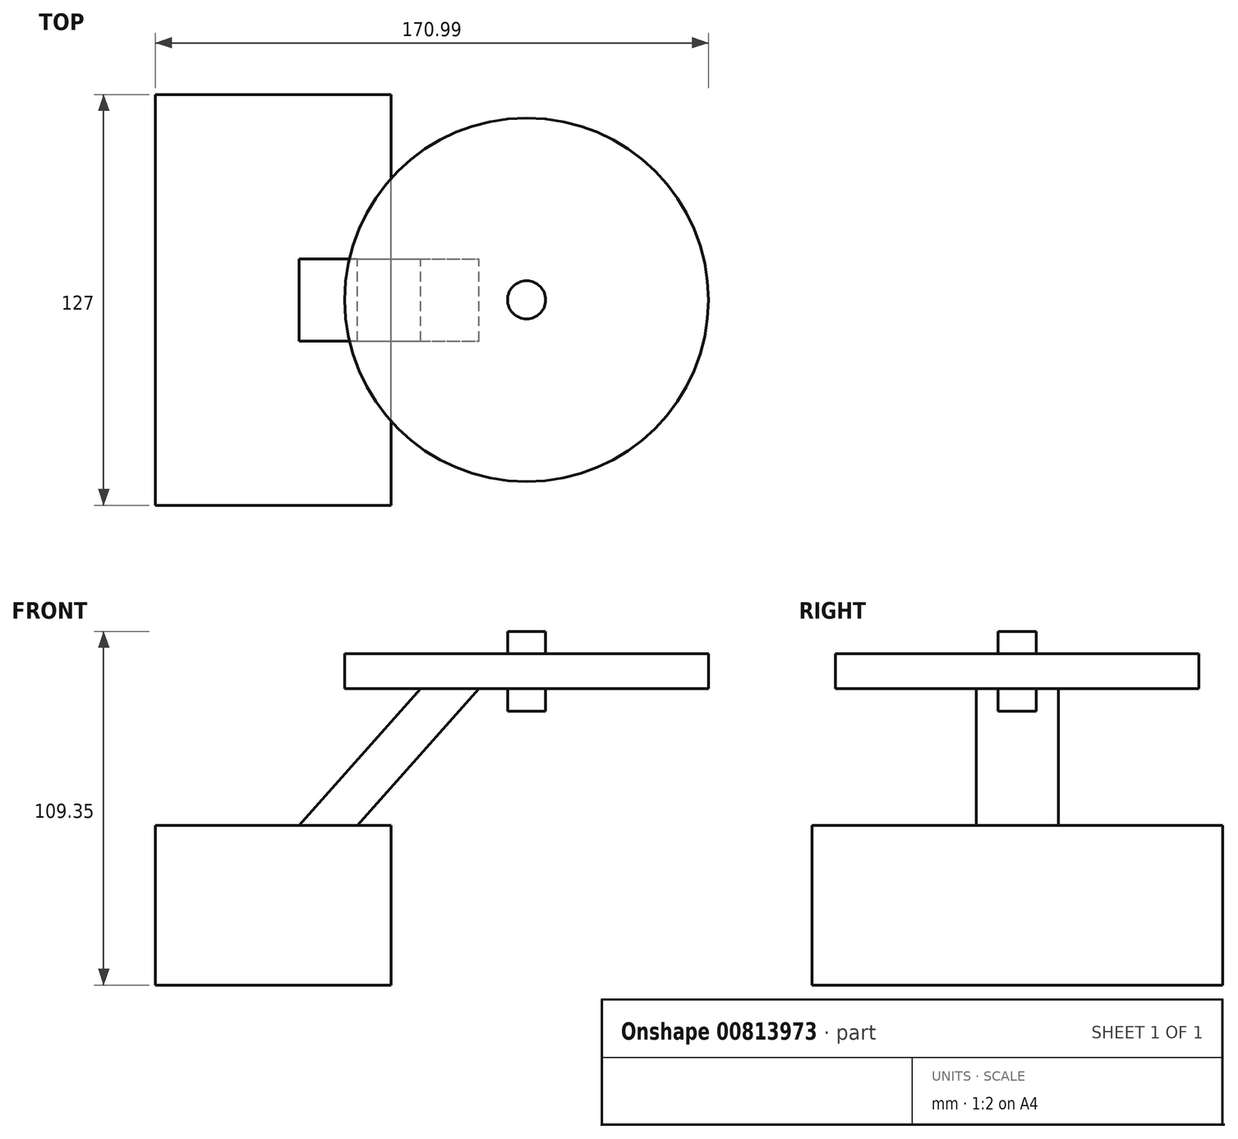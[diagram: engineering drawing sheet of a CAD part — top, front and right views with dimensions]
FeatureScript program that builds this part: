
annotation { "Feature Type Name" : "Feature", "Feature Type Description" : "" }
export const myFeature = defineFeature(function(context is Context, id is Id, definition is map)
    precondition{}
    {
        {
            var Q0;
            Q0=qCreatedBy(makeId("Front.planeOp"),FACE);
            var sketch = newSketch(context, id + "F0", { "sketchPlane" : qUnion([Q0])});
            skLineSegment(sketch, "E0.bottom", {"start": v(36.4, 24.7) * mm, "end": v(-36.4, 24.7) * mm});
            skLineSegment(sketch, "E0.top", {"start": v(36.4, -24.7) * mm, "end": v(-36.4, -24.7) * mm});
            skLineSegment(sketch, "E0.left", {"start": v(36.4, 24.7) * mm, "end": v(36.4, -24.7) * mm});
            skLineSegment(sketch, "E0.right", {"start": v(-36.4, 24.7) * mm, "end": v(-36.4, -24.7) * mm});
            skPoint(sketch, "E0.middle", {"position": v(0, 0) * mm});
            skLineSegment(sketch, "E1.bottom", {"start": v(22.1, 66.97) * mm, "end": v(134.58, 66.97) * mm});
            skLineSegment(sketch, "E1.top", {"start": v(22.1, 77.7) * mm, "end": v(134.58, 77.7) * mm});
            skLineSegment(sketch, "E1.left", {"start": v(22.1, 66.97) * mm, "end": v(22.1, 77.7) * mm});
            skLineSegment(sketch, "E1.right", {"start": v(134.58, 66.97) * mm, "end": v(134.58, 77.7) * mm});
            skPoint(sketch, "E1.middle", {"position": v(78.35, 72.33) * mm});
            skLineSegment(sketch, "E2.bottom", {"start": v(72.46, 60.01) * mm, "end": v(84.23, 60.01) * mm});
            skLineSegment(sketch, "E2.top", {"start": v(72.46, 84.65) * mm, "end": v(84.23, 84.65) * mm});
            skLineSegment(sketch, "E2.left", {"start": v(72.46, 60.01) * mm, "end": v(72.46, 84.65) * mm});
            skLineSegment(sketch, "E2.right", {"start": v(84.23, 60.01) * mm, "end": v(84.23, 84.65) * mm});
            skLineSegment(sketch, "E3", {"start": v(8.01, 24.7) * mm, "end": v(49.99, 71.86) * mm});
            skLineSegment(sketch, "E4", {"start": v(23.07, 21.37) * mm, "end": v(65.05, 68.53) * mm});
            skLineSegment(sketch, "E5", {"start": v(78.35, 60.01) * mm, "end": v(78.35, 72.33) * mm});
            skLineSegment(sketch, "E6", {"start": v(78.35, 72.33) * mm, "end": v(78.35, 84.65) * mm});
            skSolve(sketch);
        }
        {
            var Q0;
            Q0=makeQuery(id+"F0.imprint","IMPRINT",FACE,{"disambiguationData":[TD([[makeQuery(id+"F0.imprint","IMPRINT",EDGE,{"derivedFrom":sQuery(id+"F0.wireOp",EDGE,"E0.top")}),-1.0]])]});
            extrude(context, id + "F1", {"entities" : qUnion([Q0]), "endBound" : BoundingType.SYMMETRIC, "depth" : 127 * mm, "offsetDistance" : 25.4 * mm});
        }
        {
            var Q0;
            {var subQ0=sQuery(id+"F0.wireOp",EDGE,"E3");var subQ1=sQuery(id+"F0.wireOp",EDGE,"E0.bottom");var subQ2=makeQuery(id+"F0.imprint","INTERSECT",VERTEX,{"derivedFrom":[subQ1,subQ0]});Q0=makeQuery(id+"F0.imprint","IMPRINT",FACE,{"disambiguationData":[TD([[makeQuery(id+"F0.imprint","IMPRINT",EDGE,{"disambiguationData":[TD([[subQ2,1.0]])],"derivedFrom":subQ1}),-1.0]])]});}
            extrude(context, id + "F2", {"entities" : qUnion([Q0]), "operationType" : NewBodyOperationType.ADD, "endBound" : BoundingType.SYMMETRIC, "depth" : 25.4 * mm, "offsetDistance" : 25.4 * mm});
        }
        {
            var Q0;
            {var subQ0=sQuery(id+"F0.wireOp",EDGE,"E1.right");Q0=makeQuery(id+"F0.imprint","IMPRINT",FACE,{"disambiguationData":[TD([[makeQuery(id+"F0.imprint","IMPRINT",EDGE,{"derivedFrom":subQ0}),1.0]])]});}
            var Q1;
            {var subQ3=sQuery(id+"F0.wireOp",EDGE,"E1.bottom");var subQ5=sQuery(id+"F0.wireOp",EDGE,"E2.right");var subQ6=makeQuery(id+"F0.imprint","INTERSECT",VERTEX,{"derivedFrom":[subQ3,subQ5]});Q1=makeQuery(id+"F0.imprint","IMPRINT",FACE,{"disambiguationData":[TD([[makeQuery(id+"F0.imprint","IMPRINT",EDGE,{"disambiguationData":[TD([[subQ6,1.0]])],"derivedFrom":subQ3}),1.0]])]});}
            var Q2;
            {var subQ0=sQuery(id+"F0.wireOp",EDGE,"E2.right");var subQ1=sQuery(id+"F0.wireOp",EDGE,"E1.bottom");var subQ2=makeQuery(id+"F0.imprint","INTERSECT",VERTEX,{"derivedFrom":[subQ1,subQ0]});Q2=makeQuery(id+"F0.imprint","IMPRINT",FACE,{"disambiguationData":[TD([[makeQuery(id+"F0.imprint","IMPRINT",EDGE,{"disambiguationData":[TD([[subQ2,1.0]])],"derivedFrom":subQ1}),-1.0]])]});}
            var Q3;
            {var subQ0=sQuery(id+"F0.wireOp",EDGE,"E2.right");var subQ1=sQuery(id+"F0.wireOp",EDGE,"E1.top");var subQ2=makeQuery(id+"F0.imprint","INTERSECT",VERTEX,{"derivedFrom":[subQ1,subQ0]});Q3=makeQuery(id+"F0.imprint","IMPRINT",FACE,{"disambiguationData":[TD([[makeQuery(id+"F0.imprint","IMPRINT",EDGE,{"disambiguationData":[TD([[subQ2,1.0]])],"derivedFrom":subQ1}),1.0]])]});}
            var Q4;
            Q4=sQuery(id+"F0.wireOp",EDGE,"E6");
            revolve(context, id + "F3", {"operationType" : NewBodyOperationType.ADD, "surfaceOperationType" : NewSurfaceOperationType.NEW, "entities" : qUnion([Q0, Q1, Q2, Q3]), "axis" : qUnion([Q4]), "revolveType" : RevolveType.FULL});
        }
    });
